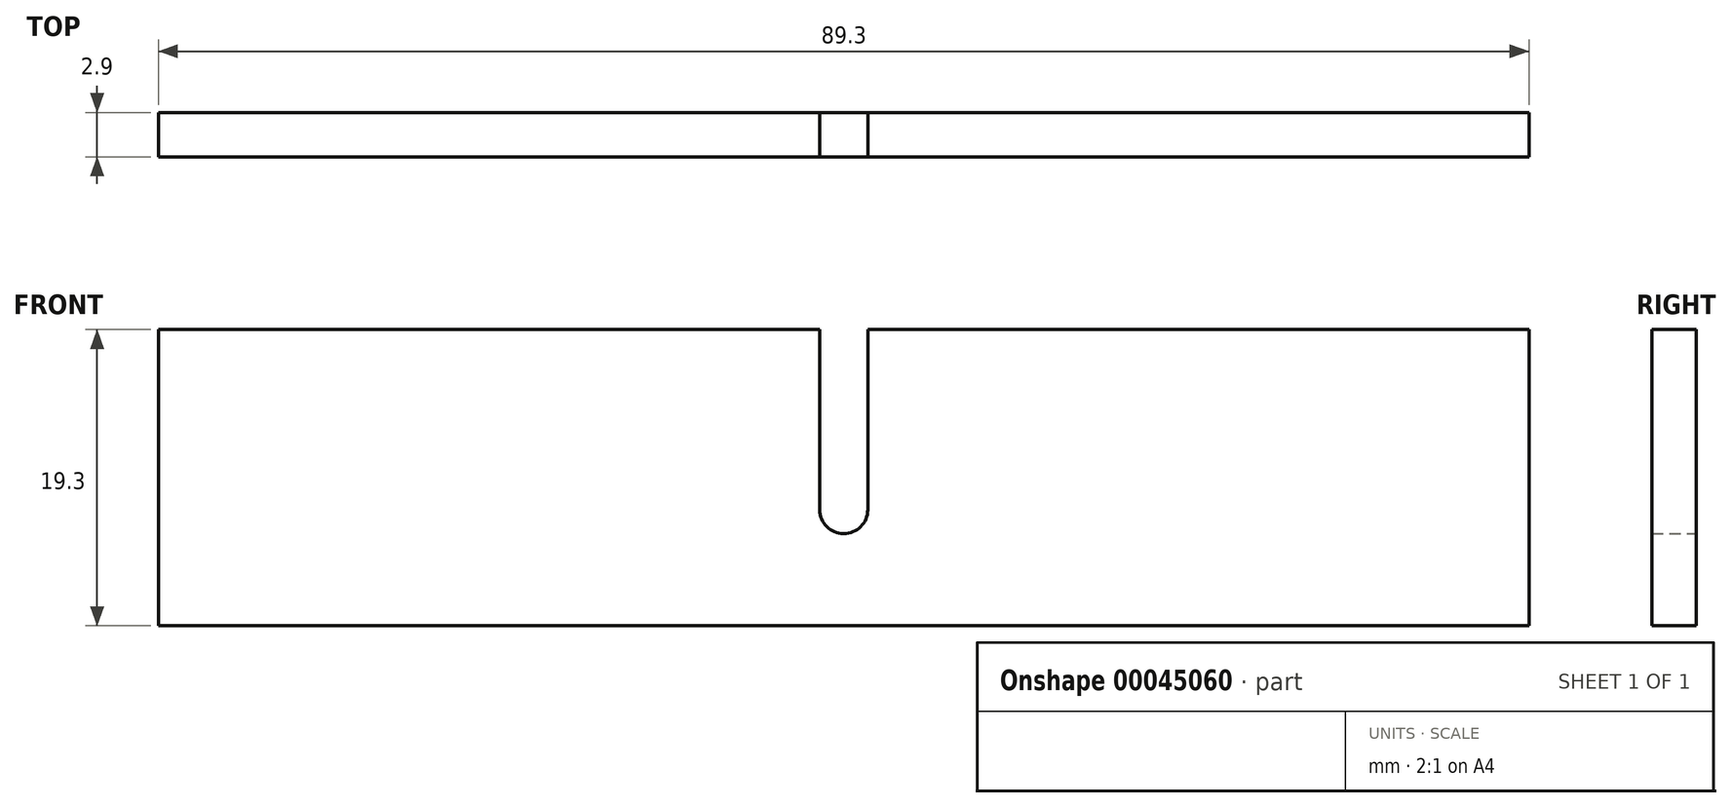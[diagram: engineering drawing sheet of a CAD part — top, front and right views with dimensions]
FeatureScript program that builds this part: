
annotation { "Feature Type Name" : "Feature", "Feature Type Description" : "" }
export const myFeature = defineFeature(function(context is Context, id is Id, definition is map)
    precondition{}
    {
        {
            var Q0;
            Q0=qCreatedBy(makeId("Front.planeOp"),FACE);
            var sketch = newSketch(context, id + "F0", { "sketchPlane" : qUnion([Q0])});
            skLineSegment(sketch, "E0", {"start": v(0, 0) * mm, "end": v(89.3, 0) * mm});
            skLineSegment(sketch, "E1", {"start": v(89.3, 0) * mm, "end": v(89.3, 19.3) * mm});
            skLineSegment(sketch, "E2", {"start": v(89.3, 19.3) * mm, "end": v(46.2, 19.3) * mm});
            skLineSegment(sketch, "E3", {"start": v(46.2, 19.3) * mm, "end": v(46.2, 7.56) * mm});
            skArc(sketch, "E4", {"start": v(46.2, 7.56) * mm, "mid": v(44.65, 6) * mm, "end": v(43.1, 7.56) * mm});
            skLineSegment(sketch, "E5", {"start": v(43.1, 7.56) * mm, "end": v(43.1, 19.3) * mm});
            skLineSegment(sketch, "E6", {"start": v(43.1, 19.3) * mm, "end": v(0, 19.3) * mm});
            skLineSegment(sketch, "E7", {"start": v(0, 19.3) * mm, "end": v(0, 0) * mm});
            skPoint(sketch, "E8", {"position": v(44.65, 6) * mm});
            skPoint(sketch, "E9", {"position": v(44.65, 0) * mm});
            skSolve(sketch);
        }
        {
            var Q0;
            Q0 = qSketchRegion(id + "F0", true);
            extrude(context, id + "F1", {"entities" : qUnion([Q0]), "depth" : 2.9 * mm});
        }
    });
